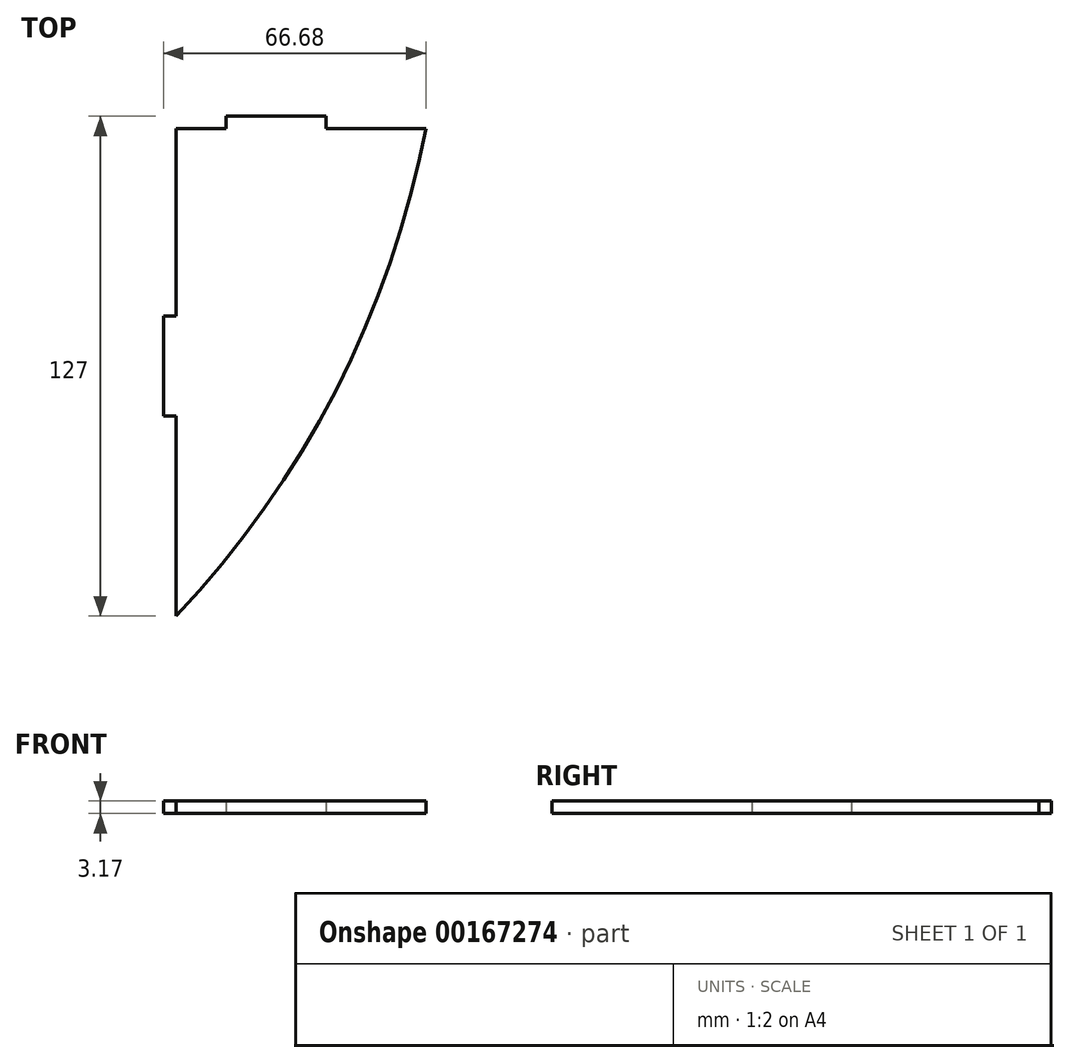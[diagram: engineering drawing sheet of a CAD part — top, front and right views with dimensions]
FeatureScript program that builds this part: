
annotation { "Feature Type Name" : "Feature", "Feature Type Description" : "" }
export const myFeature = defineFeature(function(context is Context, id is Id, definition is map)
    precondition{}
    {
        {
            var Q0;
            Q0=qCreatedBy(makeId("Top.planeOp"),FACE);
            var sketch = newSketch(context, id + "F0", { "sketchPlane" : qUnion([Q0])});
            skLineSegment(sketch, "E0.bottom", {"start": v(-22.23, 63.5) * mm, "end": v(3.17, 63.5) * mm});
            skLineSegment(sketch, "E1", {"start": v(-34.92, 60.32) * mm, "end": v(-22.23, 60.32) * mm});
            skLineSegment(sketch, "E2", {"start": v(-34.92, 60.32) * mm, "end": v(-34.92, 12.7) * mm});
            skLineSegment(sketch, "E3.bottom", {"start": v(-34.92, 12.7) * mm, "end": v(-38.1, 12.7) * mm});
            skLineSegment(sketch, "E3.top", {"start": v(-34.92, -12.7) * mm, "end": v(-38.1, -12.7) * mm});
            skLineSegment(sketch, "E3.right", {"start": v(-38.1, 12.7) * mm, "end": v(-38.1, -12.7) * mm});
            skLineSegment(sketch, "E4.top", {"start": v(3.17, 63.5) * mm, "end": v(-22.23, 63.5) * mm});
            skLineSegment(sketch, "E4.left", {"start": v(3.17, 60.32) * mm, "end": v(3.17, 63.5) * mm});
            skLineSegment(sketch, "E4.right", {"start": v(-22.23, 60.32) * mm, "end": v(-22.23, 63.5) * mm});
            skLineSegment(sketch, "E5", {"start": v(-34.92, -60.32) * mm, "end": v(-34.92, -63.5) * mm});
            skLineSegment(sketch, "E6.trimOffspring", {"start": v(-34.92, -12.7) * mm, "end": v(-34.92, -60.32) * mm});
            skLineSegment(sketch, "E7", {"start": v(3.17, 60.32) * mm, "end": v(28.58, 60.32) * mm});
            skArc(sketch, "E8", {"start": v(-34.92, -63.5) * mm, "mid": v(5.72, -6.15) * mm, "end": v(28.58, 60.32) * mm});
            skSolve(sketch);
        }
        {
            var Q0;
            Q0=makeQuery(id+"F0.imprint","IMPRINT",FACE,{"disambiguationData":[TD([[makeQuery(id+"F0.imprint","IMPRINT",EDGE,{"derivedFrom":sQuery(id+"F0.wireOp",EDGE,"E1")}),-1.0]])]});
            extrude(context, id + "F1", {"entities" : qUnion([Q0]), "depth" : 3.17 * mm});
        }
    });
